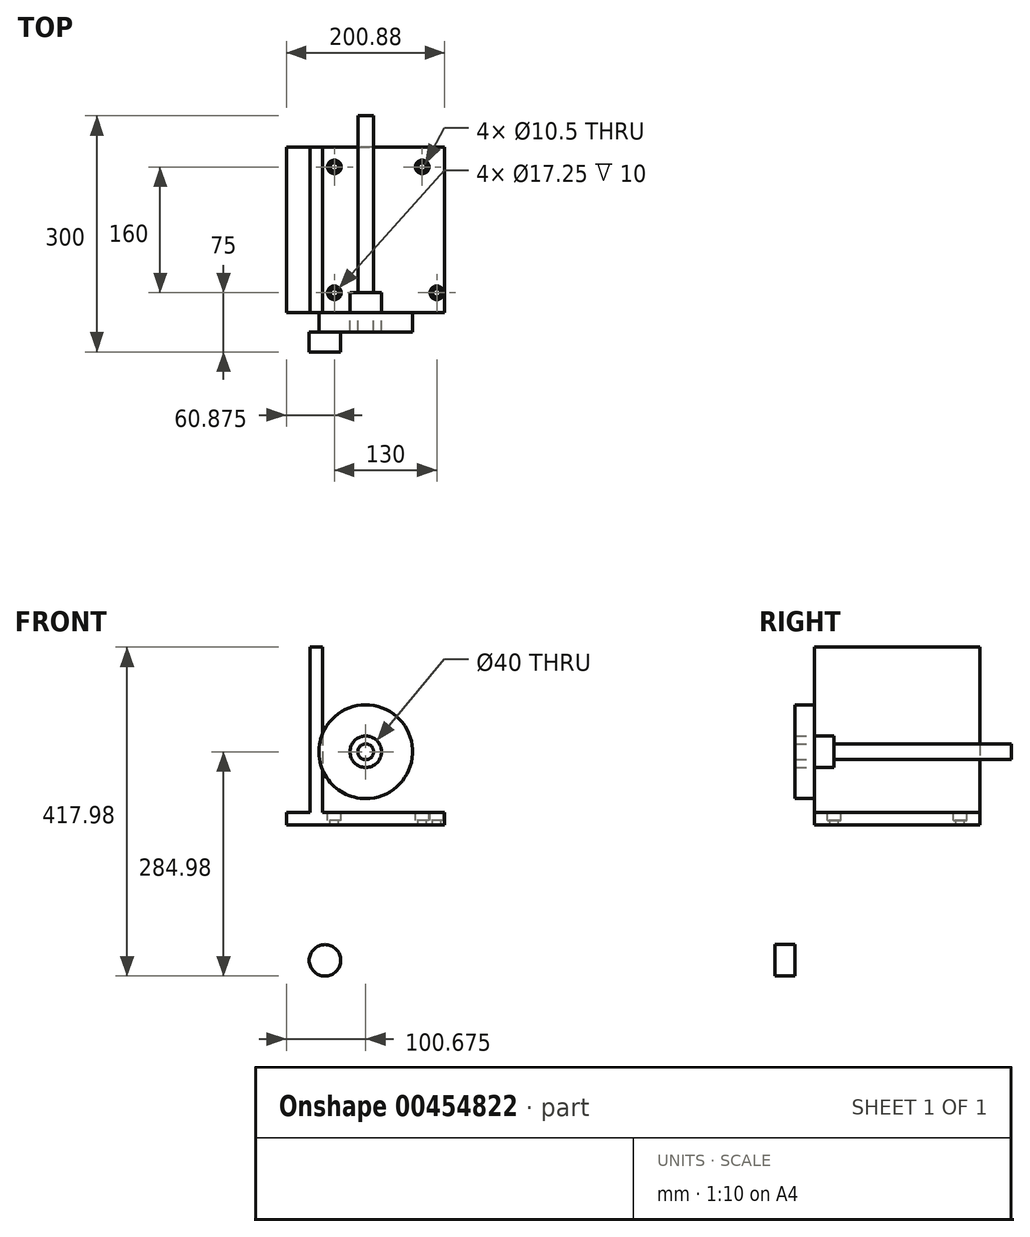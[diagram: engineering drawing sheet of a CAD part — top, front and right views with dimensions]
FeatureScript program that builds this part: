
annotation { "Feature Type Name" : "Feature", "Feature Type Description" : "" }
export const myFeature = defineFeature(function(context is Context, id is Id, definition is map)
    precondition{}
    {
        {
            var Q0;
            Q0=qCreatedBy(makeId("Front.planeOp"),FACE);
            var sketch = newSketch(context, id + "F0", { "sketchPlane" : qUnion([Q0])});
            skLineSegment(sketch, "E0", {"start": v(0, 0) * mm, "end": v(0, 210) * mm});
            skLineSegment(sketch, "E1", {"start": v(0, 210) * mm, "end": v(15.87, 210) * mm});
            skLineSegment(sketch, "E2", {"start": v(15.88, 210) * mm, "end": v(15.88, 0) * mm});
            skLineSegment(sketch, "E3", {"start": v(15.88, 0) * mm, "end": v(170.88, 0) * mm});
            skLineSegment(sketch, "E4", {"start": v(170.88, 0) * mm, "end": v(170.88, -15.88) * mm});
            skLineSegment(sketch, "E5", {"start": v(170.88, -15.87) * mm, "end": v(-30, -15.88) * mm});
            skLineSegment(sketch, "E6", {"start": v(-30, -15.88) * mm, "end": v(-30, 0) * mm});
            skLineSegment(sketch, "E7", {"start": v(-30, 0) * mm, "end": v(0, 0) * mm});
            skSolve(sketch);
        }
        {
            var Q0;
            Q0=makeQuery(id+"F0.imprint","IMPRINT",FACE,{"disambiguationData":[TD([[makeQuery(id+"F0.imprint","IMPRINT",EDGE,{"derivedFrom":sQuery(id+"F0.wireOp",EDGE,"E0")}),-1.0]])]});
            extrude(context, id + "F1", {"entities" : qUnion([Q0]), "oppositeDirection" : true, "depth" : 210 * mm});
        }
        {
            var Q0;
            Q0=makeQuery(id+"F1.opExtrude","SWEPT_FACE",FACE,{"disambiguationData":[OSD([sQuery(id+"F0.wireOp",EDGE,"E3")])]});
            var sketch = newSketch(context, id + "F2", { "sketchPlane" : qUnion([Q0])});
            skPoint(sketch, "E8", {"position": v(142.36, 185) * mm});
            skPoint(sketch, "E9", {"position": v(30.87, 185) * mm});
            skPoint(sketch, "E10", {"position": v(30.88, 25) * mm});
            skPoint(sketch, "E11", {"position": v(160.88, 25) * mm});
            skSolve(sketch);
        }
        {
            var Q0;
            Q0=sQuery(id+"F2.wireOp",VERTEX,"E10");
            var Q1;
            Q1=sQuery(id+"F2.wireOp",VERTEX,"E11");
            var Q2;
            Q2=sQuery(id+"F2.wireOp",VERTEX,"E8");
            var Q3;
            Q3=sQuery(id+"F2.wireOp",VERTEX,"E9");
            var Q4;
            Q4=makeQuery(id+"F1.opExtrude","SWEPT_BODY",BODY,{"disambiguationData":[OSD([sQuery(id+"F0.wireOp",EDGE,"E0"),sQuery(id+"F0.wireOp",EDGE,"E1"),sQuery(id+"F0.wireOp",EDGE,"E2"),sQuery(id+"F0.wireOp",EDGE,"E3"),sQuery(id+"F0.wireOp",EDGE,"E4"),sQuery(id+"F0.wireOp",EDGE,"E5"),sQuery(id+"F0.wireOp",EDGE,"E6"),sQuery(id+"F0.wireOp",EDGE,"E7")])]});
            hole(context, id + "F3", {"style" : HoleStyle.C_BORE, "endStyle" : HoleEndStyle.THROUGH, "standardTappedOrClearance" : lookupTablePath({ "standard" : "ISO", "fit" : "Close", "size" : "M10", "type" : "Clearance" }), "standardBlindInLast" : lookupTablePath({ "fit" : "Close", "standard" : "ISO", "size" : "M10", "type" : "Clearance" }), "holeDiameter" : 10.5 * mm, "cBoreDiameter" : 17.25 * mm, "cBoreDepth" : 10 * mm, "isTappedThrough" : true, "tappedDepth" : 12 * mm, "tapClearance" : 3, "locations" : qUnion([Q0, Q1, Q2, Q3]), "scope" : qUnion([Q4])});
        }
        {
            var Q0;
            Q0=makeQuery(id+"F1.opExtrude","CAP_FACE",FACE,{"disambiguationData":[OSD([sQuery(id+"F0.wireOp",EDGE,"E0"),sQuery(id+"F0.wireOp",EDGE,"E1"),sQuery(id+"F0.wireOp",EDGE,"E2"),sQuery(id+"F0.wireOp",EDGE,"E3"),sQuery(id+"F0.wireOp",EDGE,"E4"),sQuery(id+"F0.wireOp",EDGE,"E5"),sQuery(id+"F0.wireOp",EDGE,"E6"),sQuery(id+"F0.wireOp",EDGE,"E7")])],"isStart":true});
            var sketch = newSketch(context, id + "F4", { "sketchPlane" : qUnion([Q0])});
            skCircle(sketch, "E12", {"center": v(70.68, 77) * mm, "radius": 10 * mm});
            skCircle(sketch, "E13", {"center": v(70.68, 77) * mm, "radius": 20 * mm});
            skCircle(sketch, "E14", {"center": v(70.68, 77) * mm, "radius": 59.5 * mm});
            skPoint(sketch, "E15", {"position": v(90.68, 77) * mm});
            skPoint(sketch, "E16", {"position": v(70.68, 97) * mm});
            skSolve(sketch);
        }
        {
            var Q0;
            {var subQ0=sQuery(id+"F4.wireOp",EDGE,"E14");var subQ1=makeQuery(id+"F1.opExtrude","CAP_EDGE",EDGE,{"disambiguationData":[OSD([sQuery(id+"F0.wireOp",EDGE,"E2")])],"isStart":true});var subQ2=makeQuery(id+"F4.imprint","INTERSECT",VERTEX,{"disambiguationData":[OD(0.0)],"derivedFrom":[subQ1,subQ0]});Q0=makeQuery(id+"F4.imprint","IMPRINT",FACE,{"disambiguationData":[TD([[makeQuery(id+"F4.imprint","IMPRINT",EDGE,{"disambiguationData":[TD([[subQ2,-1.0]])],"derivedFrom":subQ0}),1.0]])]});}
            var Q1;
            Q1=makeQuery(id+"F4.imprint","IMPRINT",FACE,{"disambiguationData":[TD([[makeQuery(id+"F4.imprint","IMPRINT",EDGE,{"derivedFrom":sQuery(id+"F4.wireOp",EDGE,"E13")}),-1.0]])]});
            extrude(context, id + "F5", {"entities" : qUnion([Q0, Q1]), "operationType" : NewBodyOperationType.ADD, "depth" : 25 * mm});
        }
        {
            var Q0;
            Q0=makeQuery(id+"F4.imprint","IMPRINT",FACE,{"disambiguationData":[TD([[makeQuery(id+"F4.imprint","IMPRINT",EDGE,{"derivedFrom":sQuery(id+"F4.wireOp",EDGE,"E12")}),-1.0]])]});
            extrude(context, id + "F6", {"entities" : qUnion([Q0]), "operationType" : NewBodyOperationType.ADD, "oppositeDirection" : true, "depth" : 25 * mm});
        }
        {
            var Q0;
            Q0=makeQuery(id+"F4.imprint","IMPRINT",FACE,{"disambiguationData":[TD([[makeQuery(id+"F4.imprint","IMPRINT",EDGE,{"derivedFrom":sQuery(id+"F4.wireOp",EDGE,"E12")}),1.0]])]});
            extrude(context, id + "F7", {"entities" : qUnion([Q0]), "operationType" : NewBodyOperationType.ADD, "depth" : 25 * mm, "hasSecondDirection" : true, "secondDirectionOppositeDirection" : true, "secondDirectionDepth" : 250 * mm});
        }
        {
            var Q0;
            Q0=makeQuery(id+"F7.opExtrude","CAP_FACE",FACE,{"disambiguationData":[OSD([sQuery(id+"F4.wireOp",EDGE,"E12")])],"isStart":false});
            var sketch = newSketch(context, id + "F8", { "sketchPlane" : qUnion([Q0])});
            skCircle(sketch, "E17", {"center": v(18.87, -187.98) * mm, "radius": 20 * mm});
            skCircle(sketch, "E18.0", {"center": v(70.68, 77) * mm, "radius": 10 * mm});
            skSolve(sketch);
        }
        {
            var Q0;
            Q0=makeQuery(id+"F8.imprint","IMPRINT",FACE,{"disambiguationData":[TD([[makeQuery(id+"F8.imprint","IMPRINT",EDGE,{"derivedFrom":sQuery(id+"F8.wireOp",EDGE,"E17")}),1.0]])]});
            extrude(context, id + "F9", {"entities" : qUnion([Q0]), "depth" : 25 * mm});
        }
    });
